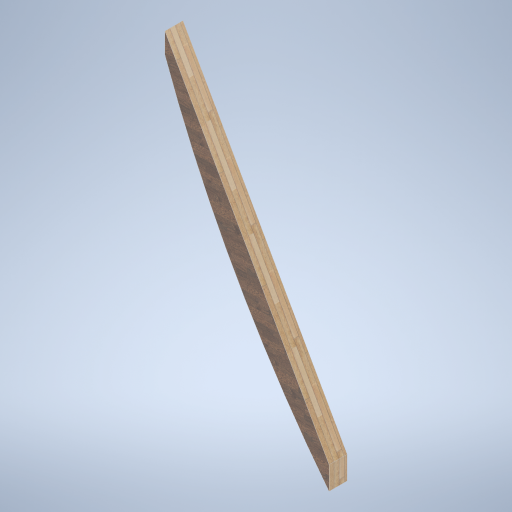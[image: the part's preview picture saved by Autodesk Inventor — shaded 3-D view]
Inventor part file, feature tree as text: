
AUTODESK INVENTOR PART (.ipt)
format: ipt  version: 2024.2 (Build 282272000, 272)  size: 294,912 bytes
history: native  units: in
note: dims shown in document units (in); Inventor stores cm internally (conversion verified against a paired STEP export)
features: other x3, sketch x1
ambient origin geometry x8: Origin, YZ Plane, XZ Plane, XY Plane, X Axis, Y Axis, Z Axis, Center Point
bodies: Body1 (feature_tree)
feature tree (4):
  other  "side_curve_beam_04.ipt"
  other  "Solid2::side_curve_beam_04.ipt"
  other  "TaggingFeature1"
  sketch  "Sketch1"  dims[d0=0.3937in]
